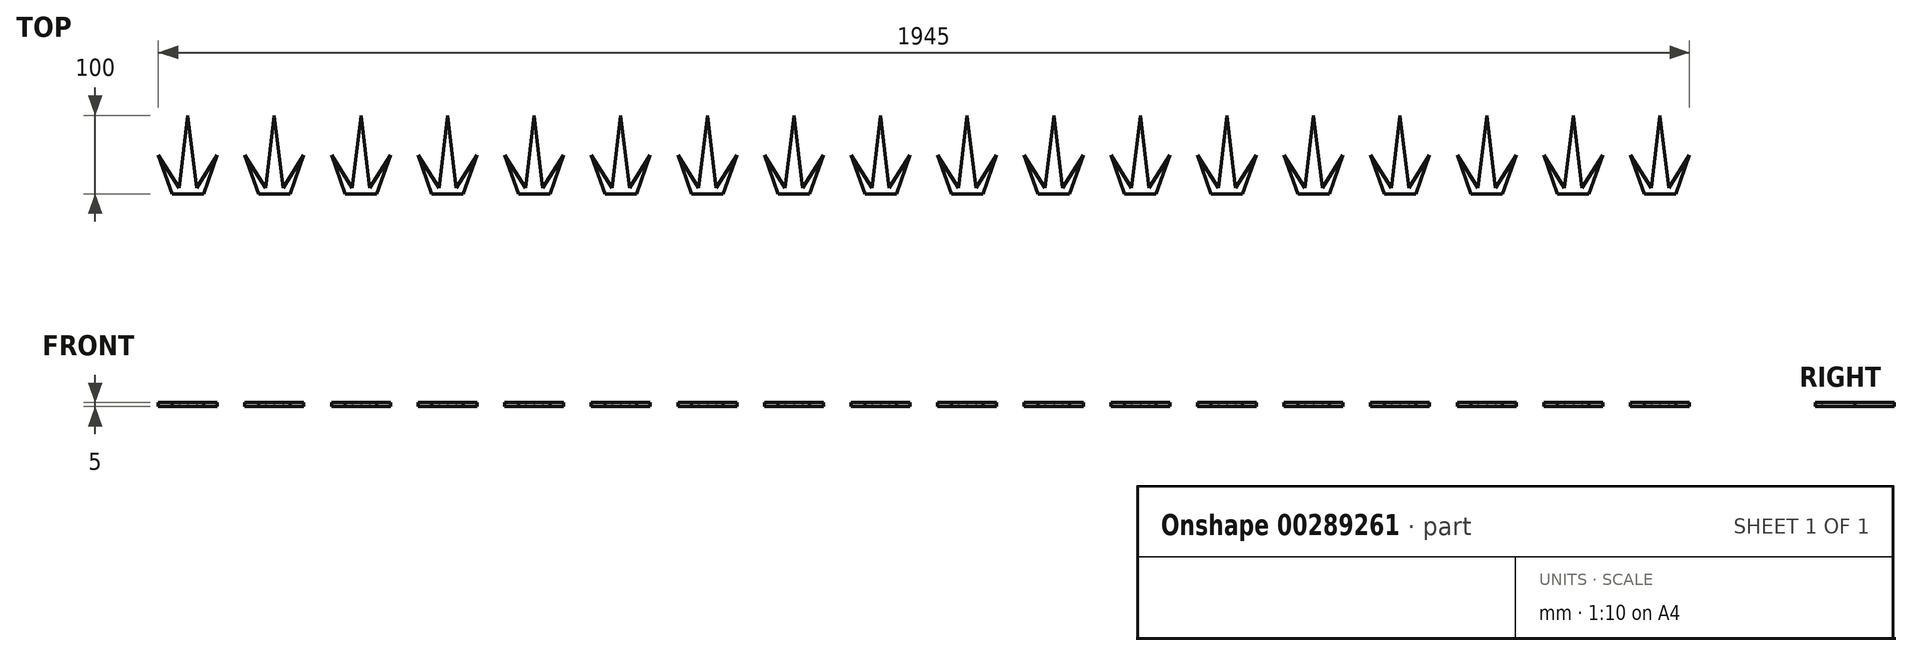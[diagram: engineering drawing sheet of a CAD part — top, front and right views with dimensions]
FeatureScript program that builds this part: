
annotation { "Feature Type Name" : "Feature", "Feature Type Description" : "" }
export const myFeature = defineFeature(function(context is Context, id is Id, definition is map)
    precondition{}
    {
        {
            var Q0;
            Q0=qCreatedBy(makeId("Top.planeOp"),FACE);
            var sketch = newSketch(context, id + "F0", { "sketchPlane" : qUnion([Q0])});
            skLineSegment(sketch, "E0", {"start": v(0, 0) * mm, "end": v(0, 69.74) * mm, "construction": true});
            skLineSegment(sketch, "E1", {"start": v(0, 0) * mm, "end": v(-20, 0) * mm});
            skLineSegment(sketch, "E2", {"start": v(-20, 0) * mm, "end": v(-37.5, 49.84) * mm});
            skLineSegment(sketch, "E3", {"start": v(-37.5, 49.84) * mm, "end": v(-11.04, 7.97) * mm});
            skLineSegment(sketch, "E4", {"start": v(-11.04, 7.97) * mm, "end": v(0, 100) * mm});
            skLineSegment(sketch, "E5.MirrorCS", {"start": v(0, 0) * mm, "end": v(20, 0) * mm});
            skLineSegment(sketch, "E6.MirrorCS", {"start": v(11.04, 7.97) * mm, "end": v(0, 100) * mm});
            skLineSegment(sketch, "E7.MirrorCS", {"start": v(37.5, 49.84) * mm, "end": v(11.04, 7.97) * mm});
            skLineSegment(sketch, "E8.MirrorCS", {"start": v(20, 0) * mm, "end": v(37.5, 49.84) * mm});
            skLineSegment(sketch, "E9.1.0.0", {"start": v(72.5, 49.84) * mm, "end": v(98.96, 7.97) * mm});
            skLineSegment(sketch, "E9.1.0.1", {"start": v(147.5, 49.84) * mm, "end": v(121.04, 7.97) * mm});
            skLineSegment(sketch, "E9.1.0.2", {"start": v(130, 0) * mm, "end": v(147.5, 49.84) * mm});
            skLineSegment(sketch, "E9.1.0.3", {"start": v(110, 0) * mm, "end": v(90, 0) * mm});
            skLineSegment(sketch, "E9.1.0.4", {"start": v(121.04, 7.97) * mm, "end": v(110, 100) * mm});
            skLineSegment(sketch, "E9.1.0.5", {"start": v(110, 0) * mm, "end": v(130, 0) * mm});
            skLineSegment(sketch, "E9.1.0.6", {"start": v(98.96, 7.97) * mm, "end": v(110, 100) * mm});
            skLineSegment(sketch, "E9.1.0.7", {"start": v(90, 0) * mm, "end": v(72.5, 49.84) * mm});
            skLineSegment(sketch, "E9.2.0.0", {"start": v(182.5, 49.84) * mm, "end": v(208.96, 7.97) * mm});
            skLineSegment(sketch, "E9.2.0.1", {"start": v(257.5, 49.84) * mm, "end": v(231.04, 7.97) * mm});
            skLineSegment(sketch, "E9.2.0.2", {"start": v(240, 0) * mm, "end": v(257.5, 49.84) * mm});
            skLineSegment(sketch, "E9.2.0.3", {"start": v(220, 0) * mm, "end": v(200, 0) * mm});
            skLineSegment(sketch, "E9.2.0.4", {"start": v(231.04, 7.97) * mm, "end": v(220, 100) * mm});
            skLineSegment(sketch, "E9.2.0.5", {"start": v(220, 0) * mm, "end": v(240, 0) * mm});
            skLineSegment(sketch, "E9.2.0.6", {"start": v(208.96, 7.97) * mm, "end": v(220, 100) * mm});
            skLineSegment(sketch, "E9.2.0.7", {"start": v(200, 0) * mm, "end": v(182.5, 49.84) * mm});
            skLineSegment(sketch, "E9.3.0.0", {"start": v(292.5, 49.84) * mm, "end": v(318.96, 7.97) * mm});
            skLineSegment(sketch, "E9.3.0.1", {"start": v(367.5, 49.84) * mm, "end": v(341.04, 7.97) * mm});
            skLineSegment(sketch, "E9.3.0.2", {"start": v(350, 0) * mm, "end": v(367.5, 49.84) * mm});
            skLineSegment(sketch, "E9.3.0.3", {"start": v(330, 0) * mm, "end": v(310, 0) * mm});
            skLineSegment(sketch, "E9.3.0.4", {"start": v(341.04, 7.97) * mm, "end": v(330, 100) * mm});
            skLineSegment(sketch, "E9.3.0.5", {"start": v(330, 0) * mm, "end": v(350, 0) * mm});
            skLineSegment(sketch, "E9.3.0.6", {"start": v(318.96, 7.97) * mm, "end": v(330, 100) * mm});
            skLineSegment(sketch, "E9.3.0.7", {"start": v(310, 0) * mm, "end": v(292.5, 49.84) * mm});
            skLineSegment(sketch, "E9.4.0.0", {"start": v(402.5, 49.84) * mm, "end": v(428.96, 7.97) * mm});
            skLineSegment(sketch, "E9.4.0.1", {"start": v(477.5, 49.84) * mm, "end": v(451.04, 7.97) * mm});
            skLineSegment(sketch, "E9.4.0.2", {"start": v(460, 0) * mm, "end": v(477.5, 49.84) * mm});
            skLineSegment(sketch, "E9.4.0.3", {"start": v(440, 0) * mm, "end": v(420, 0) * mm});
            skLineSegment(sketch, "E9.4.0.4", {"start": v(451.04, 7.97) * mm, "end": v(440, 100) * mm});
            skLineSegment(sketch, "E9.4.0.5", {"start": v(440, 0) * mm, "end": v(460, 0) * mm});
            skLineSegment(sketch, "E9.4.0.6", {"start": v(428.96, 7.97) * mm, "end": v(440, 100) * mm});
            skLineSegment(sketch, "E9.4.0.7", {"start": v(420, 0) * mm, "end": v(402.5, 49.84) * mm});
            skLineSegment(sketch, "E9.5.0.0", {"start": v(512.5, 49.84) * mm, "end": v(538.96, 7.97) * mm});
            skLineSegment(sketch, "E9.5.0.1", {"start": v(587.5, 49.84) * mm, "end": v(561.04, 7.97) * mm});
            skLineSegment(sketch, "E9.5.0.2", {"start": v(570, 0) * mm, "end": v(587.5, 49.84) * mm});
            skLineSegment(sketch, "E9.5.0.3", {"start": v(550, 0) * mm, "end": v(530, 0) * mm});
            skLineSegment(sketch, "E9.5.0.4", {"start": v(561.04, 7.97) * mm, "end": v(550, 100) * mm});
            skLineSegment(sketch, "E9.5.0.5", {"start": v(550, 0) * mm, "end": v(570, 0) * mm});
            skLineSegment(sketch, "E9.5.0.6", {"start": v(538.96, 7.97) * mm, "end": v(550, 100) * mm});
            skLineSegment(sketch, "E9.5.0.7", {"start": v(530, 0) * mm, "end": v(512.5, 49.84) * mm});
            skLineSegment(sketch, "E9.6.0.0", {"start": v(622.5, 49.84) * mm, "end": v(648.96, 7.97) * mm});
            skLineSegment(sketch, "E9.6.0.1", {"start": v(697.5, 49.84) * mm, "end": v(671.04, 7.97) * mm});
            skLineSegment(sketch, "E9.6.0.2", {"start": v(680, 0) * mm, "end": v(697.5, 49.84) * mm});
            skLineSegment(sketch, "E9.6.0.3", {"start": v(660, 0) * mm, "end": v(640, 0) * mm});
            skLineSegment(sketch, "E9.6.0.4", {"start": v(671.04, 7.97) * mm, "end": v(660, 100) * mm});
            skLineSegment(sketch, "E9.6.0.5", {"start": v(660, 0) * mm, "end": v(680, 0) * mm});
            skLineSegment(sketch, "E9.6.0.6", {"start": v(648.96, 7.97) * mm, "end": v(660, 100) * mm});
            skLineSegment(sketch, "E9.6.0.7", {"start": v(640, 0) * mm, "end": v(622.5, 49.84) * mm});
            skLineSegment(sketch, "E9.7.0.0", {"start": v(732.5, 49.84) * mm, "end": v(758.96, 7.97) * mm});
            skLineSegment(sketch, "E9.7.0.1", {"start": v(807.5, 49.84) * mm, "end": v(781.04, 7.97) * mm});
            skLineSegment(sketch, "E9.7.0.2", {"start": v(790, 0) * mm, "end": v(807.5, 49.84) * mm});
            skLineSegment(sketch, "E9.7.0.3", {"start": v(770, 0) * mm, "end": v(750, 0) * mm});
            skLineSegment(sketch, "E9.7.0.4", {"start": v(781.04, 7.97) * mm, "end": v(770, 100) * mm});
            skLineSegment(sketch, "E9.7.0.5", {"start": v(770, 0) * mm, "end": v(790, 0) * mm});
            skLineSegment(sketch, "E9.7.0.6", {"start": v(758.96, 7.97) * mm, "end": v(770, 100) * mm});
            skLineSegment(sketch, "E9.7.0.7", {"start": v(750, 0) * mm, "end": v(732.5, 49.84) * mm});
            skLineSegment(sketch, "E9.8.0.0", {"start": v(842.5, 49.84) * mm, "end": v(868.96, 7.97) * mm});
            skLineSegment(sketch, "E9.8.0.1", {"start": v(917.5, 49.84) * mm, "end": v(891.04, 7.97) * mm});
            skLineSegment(sketch, "E9.8.0.2", {"start": v(900, 0) * mm, "end": v(917.5, 49.84) * mm});
            skLineSegment(sketch, "E9.8.0.3", {"start": v(880, 0) * mm, "end": v(860, 0) * mm});
            skLineSegment(sketch, "E9.8.0.4", {"start": v(891.04, 7.97) * mm, "end": v(880, 100) * mm});
            skLineSegment(sketch, "E9.8.0.5", {"start": v(880, 0) * mm, "end": v(900, 0) * mm});
            skLineSegment(sketch, "E9.8.0.6", {"start": v(868.96, 7.97) * mm, "end": v(880, 100) * mm});
            skLineSegment(sketch, "E9.8.0.7", {"start": v(860, 0) * mm, "end": v(842.5, 49.84) * mm});
            skLineSegment(sketch, "E9.9.0.0", {"start": v(952.5, 49.84) * mm, "end": v(978.96, 7.97) * mm});
            skLineSegment(sketch, "E9.9.0.1", {"start": v(1027.5, 49.84) * mm, "end": v(1001.04, 7.97) * mm});
            skLineSegment(sketch, "E9.9.0.2", {"start": v(1010, 0) * mm, "end": v(1027.5, 49.84) * mm});
            skLineSegment(sketch, "E9.9.0.3", {"start": v(990, 0) * mm, "end": v(970, 0) * mm});
            skLineSegment(sketch, "E9.9.0.4", {"start": v(1001.04, 7.97) * mm, "end": v(990, 100) * mm});
            skLineSegment(sketch, "E9.9.0.5", {"start": v(990, 0) * mm, "end": v(1010, 0) * mm});
            skLineSegment(sketch, "E9.9.0.6", {"start": v(978.96, 7.97) * mm, "end": v(990, 100) * mm});
            skLineSegment(sketch, "E9.9.0.7", {"start": v(970, 0) * mm, "end": v(952.5, 49.84) * mm});
            skLineSegment(sketch, "E9.10.0.0", {"start": v(1062.5, 49.84) * mm, "end": v(1088.96, 7.97) * mm});
            skLineSegment(sketch, "E9.10.0.1", {"start": v(1137.5, 49.84) * mm, "end": v(1111.04, 7.97) * mm});
            skLineSegment(sketch, "E9.10.0.2", {"start": v(1120, 0) * mm, "end": v(1137.5, 49.84) * mm});
            skLineSegment(sketch, "E9.10.0.3", {"start": v(1100, 0) * mm, "end": v(1080, 0) * mm});
            skLineSegment(sketch, "E9.10.0.4", {"start": v(1111.04, 7.97) * mm, "end": v(1100, 100) * mm});
            skLineSegment(sketch, "E9.10.0.5", {"start": v(1100, 0) * mm, "end": v(1120, 0) * mm});
            skLineSegment(sketch, "E9.10.0.6", {"start": v(1088.96, 7.97) * mm, "end": v(1100, 100) * mm});
            skLineSegment(sketch, "E9.10.0.7", {"start": v(1080, 0) * mm, "end": v(1062.5, 49.84) * mm});
            skLineSegment(sketch, "E9.11.0.0", {"start": v(1172.5, 49.84) * mm, "end": v(1198.96, 7.97) * mm});
            skLineSegment(sketch, "E9.11.0.1", {"start": v(1247.5, 49.84) * mm, "end": v(1221.04, 7.97) * mm});
            skLineSegment(sketch, "E9.11.0.2", {"start": v(1230, 0) * mm, "end": v(1247.5, 49.84) * mm});
            skLineSegment(sketch, "E9.11.0.3", {"start": v(1210, 0) * mm, "end": v(1190, 0) * mm});
            skLineSegment(sketch, "E9.11.0.4", {"start": v(1221.04, 7.97) * mm, "end": v(1210, 100) * mm});
            skLineSegment(sketch, "E9.11.0.5", {"start": v(1210, 0) * mm, "end": v(1230, 0) * mm});
            skLineSegment(sketch, "E9.11.0.6", {"start": v(1198.96, 7.97) * mm, "end": v(1210, 100) * mm});
            skLineSegment(sketch, "E9.11.0.7", {"start": v(1190, 0) * mm, "end": v(1172.5, 49.84) * mm});
            skLineSegment(sketch, "E9.12.0.0", {"start": v(1282.5, 49.84) * mm, "end": v(1308.96, 7.97) * mm});
            skLineSegment(sketch, "E9.12.0.1", {"start": v(1357.5, 49.84) * mm, "end": v(1331.04, 7.97) * mm});
            skLineSegment(sketch, "E9.12.0.2", {"start": v(1340, 0) * mm, "end": v(1357.5, 49.84) * mm});
            skLineSegment(sketch, "E9.12.0.3", {"start": v(1320, 0) * mm, "end": v(1300, 0) * mm});
            skLineSegment(sketch, "E9.12.0.4", {"start": v(1331.04, 7.97) * mm, "end": v(1320, 100) * mm});
            skLineSegment(sketch, "E9.12.0.5", {"start": v(1320, 0) * mm, "end": v(1340, 0) * mm});
            skLineSegment(sketch, "E9.12.0.6", {"start": v(1308.96, 7.97) * mm, "end": v(1320, 100) * mm});
            skLineSegment(sketch, "E9.12.0.7", {"start": v(1300, 0) * mm, "end": v(1282.5, 49.84) * mm});
            skLineSegment(sketch, "E9.13.0.0", {"start": v(1392.5, 49.84) * mm, "end": v(1418.96, 7.97) * mm});
            skLineSegment(sketch, "E9.13.0.1", {"start": v(1467.5, 49.84) * mm, "end": v(1441.04, 7.97) * mm});
            skLineSegment(sketch, "E9.13.0.2", {"start": v(1450, 0) * mm, "end": v(1467.5, 49.84) * mm});
            skLineSegment(sketch, "E9.13.0.3", {"start": v(1430, 0) * mm, "end": v(1410, 0) * mm});
            skLineSegment(sketch, "E9.13.0.4", {"start": v(1441.04, 7.97) * mm, "end": v(1430, 100) * mm});
            skLineSegment(sketch, "E9.13.0.5", {"start": v(1430, 0) * mm, "end": v(1450, 0) * mm});
            skLineSegment(sketch, "E9.13.0.6", {"start": v(1418.96, 7.97) * mm, "end": v(1430, 100) * mm});
            skLineSegment(sketch, "E9.13.0.7", {"start": v(1410, 0) * mm, "end": v(1392.5, 49.84) * mm});
            skLineSegment(sketch, "E9.14.0.0", {"start": v(1502.5, 49.84) * mm, "end": v(1528.96, 7.97) * mm});
            skLineSegment(sketch, "E9.14.0.1", {"start": v(1577.5, 49.84) * mm, "end": v(1551.04, 7.97) * mm});
            skLineSegment(sketch, "E9.14.0.2", {"start": v(1560, 0) * mm, "end": v(1577.5, 49.84) * mm});
            skLineSegment(sketch, "E9.14.0.3", {"start": v(1540, 0) * mm, "end": v(1520, 0) * mm});
            skLineSegment(sketch, "E9.14.0.4", {"start": v(1551.04, 7.97) * mm, "end": v(1540, 100) * mm});
            skLineSegment(sketch, "E9.14.0.5", {"start": v(1540, 0) * mm, "end": v(1560, 0) * mm});
            skLineSegment(sketch, "E9.14.0.6", {"start": v(1528.96, 7.97) * mm, "end": v(1540, 100) * mm});
            skLineSegment(sketch, "E9.14.0.7", {"start": v(1520, 0) * mm, "end": v(1502.5, 49.84) * mm});
            skLineSegment(sketch, "E9.15.0.0", {"start": v(1612.5, 49.84) * mm, "end": v(1638.96, 7.97) * mm});
            skLineSegment(sketch, "E9.15.0.1", {"start": v(1687.5, 49.84) * mm, "end": v(1661.04, 7.97) * mm});
            skLineSegment(sketch, "E9.15.0.2", {"start": v(1670, 0) * mm, "end": v(1687.5, 49.84) * mm});
            skLineSegment(sketch, "E9.15.0.3", {"start": v(1650, 0) * mm, "end": v(1630, 0) * mm});
            skLineSegment(sketch, "E9.15.0.4", {"start": v(1661.04, 7.97) * mm, "end": v(1650, 100) * mm});
            skLineSegment(sketch, "E9.15.0.5", {"start": v(1650, 0) * mm, "end": v(1670, 0) * mm});
            skLineSegment(sketch, "E9.15.0.6", {"start": v(1638.96, 7.97) * mm, "end": v(1650, 100) * mm});
            skLineSegment(sketch, "E9.15.0.7", {"start": v(1630, 0) * mm, "end": v(1612.5, 49.84) * mm});
            skLineSegment(sketch, "E9.16.0.0", {"start": v(1722.5, 49.84) * mm, "end": v(1748.96, 7.97) * mm});
            skLineSegment(sketch, "E9.16.0.1", {"start": v(1797.5, 49.84) * mm, "end": v(1771.04, 7.97) * mm});
            skLineSegment(sketch, "E9.16.0.2", {"start": v(1780, 0) * mm, "end": v(1797.5, 49.84) * mm});
            skLineSegment(sketch, "E9.16.0.3", {"start": v(1760, 0) * mm, "end": v(1740, 0) * mm});
            skLineSegment(sketch, "E9.16.0.4", {"start": v(1771.04, 7.97) * mm, "end": v(1760, 100) * mm});
            skLineSegment(sketch, "E9.16.0.5", {"start": v(1760, 0) * mm, "end": v(1780, 0) * mm});
            skLineSegment(sketch, "E9.16.0.6", {"start": v(1748.96, 7.97) * mm, "end": v(1760, 100) * mm});
            skLineSegment(sketch, "E9.16.0.7", {"start": v(1740, 0) * mm, "end": v(1722.5, 49.84) * mm});
            skLineSegment(sketch, "E9.17.0.0", {"start": v(1832.5, 49.84) * mm, "end": v(1858.96, 7.97) * mm});
            skLineSegment(sketch, "E9.17.0.1", {"start": v(1907.5, 49.84) * mm, "end": v(1881.04, 7.97) * mm});
            skLineSegment(sketch, "E9.17.0.2", {"start": v(1890, 0) * mm, "end": v(1907.5, 49.84) * mm});
            skLineSegment(sketch, "E9.17.0.3", {"start": v(1870, 0) * mm, "end": v(1850, 0) * mm});
            skLineSegment(sketch, "E9.17.0.4", {"start": v(1881.04, 7.97) * mm, "end": v(1870, 100) * mm});
            skLineSegment(sketch, "E9.17.0.5", {"start": v(1870, 0) * mm, "end": v(1890, 0) * mm});
            skLineSegment(sketch, "E9.17.0.6", {"start": v(1858.96, 7.97) * mm, "end": v(1870, 100) * mm});
            skLineSegment(sketch, "E9.17.0.7", {"start": v(1850, 0) * mm, "end": v(1832.5, 49.84) * mm});
            skLineSegment(sketch, "E9.direction1", {"start": v(-20, 0) * mm, "end": v(90, 0) * mm, "construction": true});
            skSolve(sketch);
        }
        {
            var Q0;
            Q0 = qSketchRegion(id + "F0", true);
            extrude(context, id + "F1", {"entities" : qUnion([Q0]), "depth" : 5 * mm});
        }
    });
